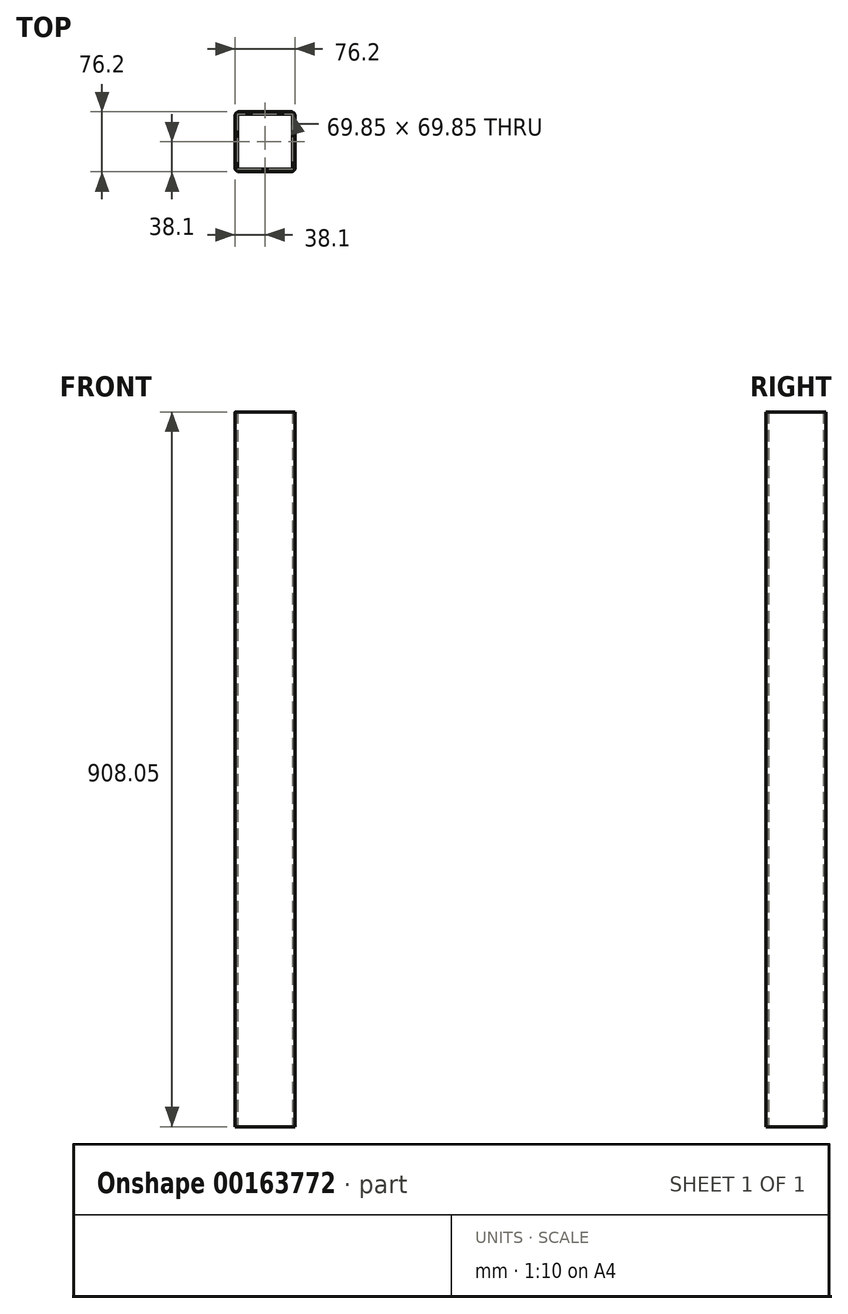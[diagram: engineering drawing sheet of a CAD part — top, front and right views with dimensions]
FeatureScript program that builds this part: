
annotation { "Feature Type Name" : "Feature", "Feature Type Description" : "" }
export const myFeature = defineFeature(function(context is Context, id is Id, definition is map)
    precondition{}
    {
        {
            var Q0;
            Q0=qCreatedBy(makeId("Top.planeOp"),FACE);
            var sketch = newSketch(context, id + "F0", { "sketchPlane" : qUnion([Q0])});
            skLineSegment(sketch, "E0.bottom", {"start": v(38.1, 38.1) * mm, "end": v(-38.1, 38.1) * mm});
            skLineSegment(sketch, "E0.top", {"start": v(38.1, -38.1) * mm, "end": v(-38.1, -38.1) * mm});
            skLineSegment(sketch, "E0.left", {"start": v(38.1, 38.1) * mm, "end": v(38.1, -38.1) * mm});
            skLineSegment(sketch, "E0.right", {"start": v(-38.1, 38.1) * mm, "end": v(-38.1, -38.1) * mm});
            skPoint(sketch, "E0.middle", {"position": v(0, 0) * mm});
            skLineSegment(sketch, "E1.0", {"start": v(34.93, 34.93) * mm, "end": v(-34.93, 34.93) * mm});
            skLineSegment(sketch, "E2.0", {"start": v(34.93, 34.93) * mm, "end": v(34.93, -34.93) * mm});
            skLineSegment(sketch, "E3.0", {"start": v(34.93, -34.93) * mm, "end": v(-34.93, -34.93) * mm});
            skLineSegment(sketch, "E4.0", {"start": v(-34.93, 34.93) * mm, "end": v(-34.93, -34.93) * mm});
            skSolve(sketch);
        }
        {
            var Q0;
            Q0=makeQuery(id+"F0.imprint","IMPRINT",FACE,{"disambiguationData":[TD([[makeQuery(id+"F0.imprint","IMPRINT",EDGE,{"derivedFrom":sQuery(id+"F0.wireOp",EDGE,"E0.bottom")}),1.0]])]});
            extrude(context, id + "F1", {"entities" : qUnion([Q0]), "depth" : 908.05 * mm, "offsetDistance" : 25.4 * mm});
        }
        {
            var Q0;
            Q0=makeQuery(id+"F1.opExtrude","SWEPT_EDGE",EDGE,{"disambiguationData":[OSD([sQuery(id+"F0.wireOp",EDGE,"E0.top"),sQuery(id+"F0.wireOp",EDGE,"E0.left")])]});
            var Q1;
            Q1=makeQuery(id+"F1.opExtrude","SWEPT_EDGE",EDGE,{"disambiguationData":[OSD([sQuery(id+"F0.wireOp",EDGE,"E0.top"),sQuery(id+"F0.wireOp",EDGE,"E0.right")])]});
            var Q2;
            Q2=makeQuery(id+"F1.opExtrude","SWEPT_EDGE",EDGE,{"disambiguationData":[OSD([sQuery(id+"F0.wireOp",EDGE,"E0.bottom"),sQuery(id+"F0.wireOp",EDGE,"E0.left")])]});
            var Q3;
            Q3=makeQuery(id+"F1.opExtrude","SWEPT_EDGE",EDGE,{"disambiguationData":[OSD([sQuery(id+"F0.wireOp",EDGE,"E0.bottom"),sQuery(id+"F0.wireOp",EDGE,"E0.right")])]});
            fillet(context, id + "F2", {"entities" : qUnion([Q0, Q1, Q2, Q3]), "radius" : 5.08 * mm, "tangentPropagation" : true, "allowEdgeOverflow" : false});
        }
    });
